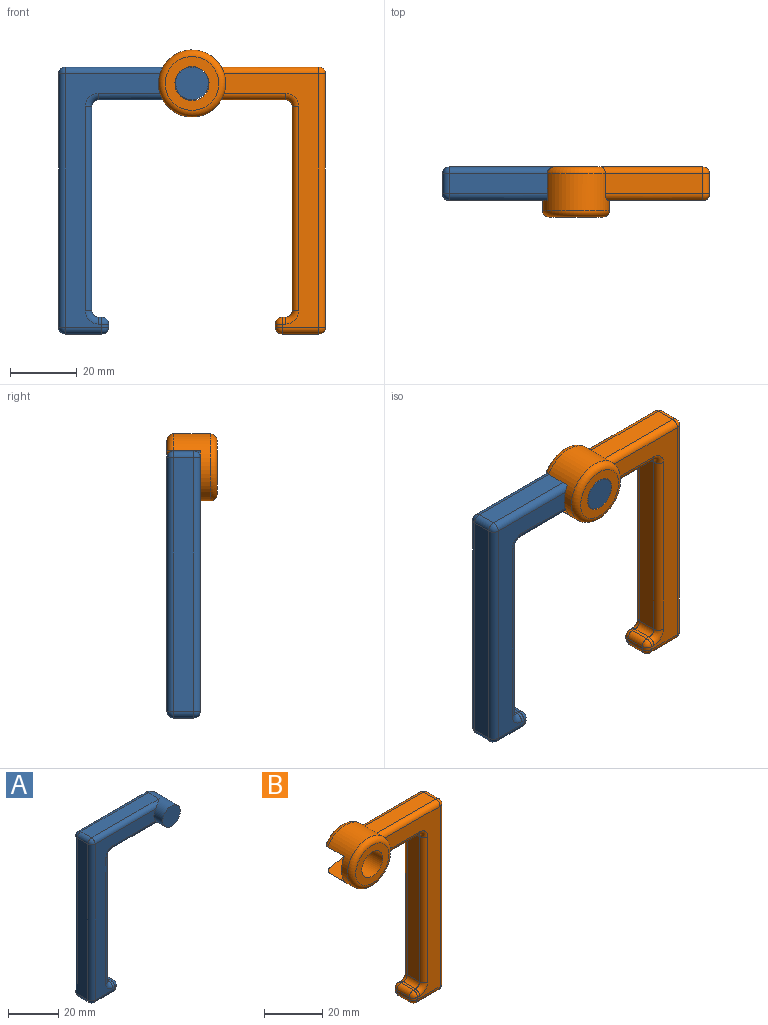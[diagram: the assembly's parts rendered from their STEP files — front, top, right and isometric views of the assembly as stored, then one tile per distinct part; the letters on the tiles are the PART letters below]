
ASSEMBLY  parts=2 mates=1
PART A: 44 faces, bbox 45.3x15x80.4 mm
  f0: cylinder r=2mm len=6mm, axis (0,1,0), area 18.8mm2, adj f1,f11,f16,f21
  f1: plane 28x6mm, normal (0,0,-1), area 168mm2, adj f0,f2,f15,f25
  f2: cylinder r=4.9mm len=13mm, axis (0,1,0), area 284.1mm2, adj f1,f3,f12,f14,f15,f17,f29
  f3: plane 38x6mm, normal (0,0,1), area 228mm2, adj f2,f4,f17,f34
  f4: cylinder r=2mm len=6mm, axis (0,1,0), area 18.8mm2, adj f3,f5,f19,f37
  f5: plane 76x6mm, normal (-1,0,0), area 456mm2, adj f4,f6,f22,f40
  f6: cylinder r=2mm len=6mm, axis (0,1,0), area 18.8mm2, adj f5,f7,f26,f42
  f7: plane 11x6mm, normal (0,0,-1), area 66mm2, adj f6,f30,f38,f43
  f8: plane 6x1mm, normal (1,0,0), area 6mm2, adj f31,f32,f38,f39
  f9: plane 6x1mm, normal (0,0,1), area 6mm2, adj f10,f23,f32,f33
  f10: cylinder r=2mm len=6mm, axis (0,1,0), area 18.8mm2, adj f9,f11,f20,f28
  f11: plane 61.2x6mm, normal (1,0,0), area 367.2mm2, adj f0,f10,f18,f24
  f12: plane 76x34.05mm, normal (0,-1,0), area 626.8mm2, adj f2,f15,f16,f17,f18,f20,f22,f23
  f13: plane 76x40.9mm, normal (0,1,0), area 666.7mm2, adj f21,f24,f25,f28,f29,f33,f34,f39
  f14: plane 9.8x9.8mm, normal (0,-1,0), area 75.4mm2, adj f2
  f15: cylinder r=2mm len=28mm, axis (-1,0,0), area 81mm2, adj f1,f2,f12,f16
  f16: torus R=4mm, axis (0,-1,0), area 13.5mm2, adj f0,f12,f15,f18
  f17: cylinder r=2mm len=38mm, axis (1,0,0), area 112.5mm2, adj f2,f3,f12,f19
  f18: cylinder r=2mm len=61.2mm, axis (0,0,-1), area 192.3mm2, adj f11,f12,f16,f20
  f19: sphere r=2mm, area 6.3mm2, adj f4,f17,f22
  f20: torus R=4mm, axis (0,-1,0), area 13.5mm2, adj f10,f12,f18,f23
  f21: torus R=4mm, axis (0,-1,0), area 13.5mm2, adj f0,f13,f24,f25
  f22: cylinder r=2mm len=76mm, axis (0,0,1), area 238.8mm2, adj f5,f12,f19,f26
  f23: cylinder r=2mm len=2mm, axis (1,0,0), area 3.1mm2, adj f9,f12,f20,f27
  f24: cylinder r=2mm len=61.2mm, axis (0,0,1), area 192.3mm2, adj f11,f13,f21,f28
  f25: cylinder r=2mm len=28mm, axis (1,0,0), area 88mm2, adj f1,f13,f21,f29
  f26: sphere r=2mm, area 6.3mm2, adj f6,f22,f30
  f27: sphere r=2mm, area 6.3mm2, adj f23,f31,f32
  f28: torus R=4mm, axis (0,-1,0), area 13.5mm2, adj f10,f13,f24,f33
  f29: torus R=2.9mm, axis (0,-1,0), area 41.2mm2, adj f2,f13,f25,f34
  f30: cylinder r=2mm len=11mm, axis (-1,0,0), area 34.6mm2, adj f7,f12,f26,f35
  f31: cylinder r=2mm len=2mm, axis (0,0,-1), area 3.1mm2, adj f8,f12,f27,f35
  f32: cylinder r=2mm len=6mm, axis (0,1,0), area 18.8mm2, adj f8,f9,f27,f36
  f33: cylinder r=2mm len=2mm, axis (-1,0,0), area 3.1mm2, adj f9,f13,f28,f36
  f34: cylinder r=2mm len=38mm, axis (-1,0,0), area 119.4mm2, adj f3,f13,f29,f37
  f35: sphere r=2mm, area 6.3mm2, adj f30,f31,f38
  f36: sphere r=2mm, area 6.3mm2, adj f32,f33,f39
  f37: sphere r=2mm, area 6.3mm2, adj f4,f34,f40
  f38: cylinder r=2mm len=6mm, axis (0,1,0), area 18.8mm2, adj f7,f8,f35,f41
  f39: cylinder r=2mm len=2mm, axis (0,0,1), area 3.1mm2, adj f8,f13,f36,f41
  f40: cylinder r=2mm len=76mm, axis (0,0,-1), area 238.8mm2, adj f5,f13,f37,f42
  f41: sphere r=2mm, area 6.3mm2, adj f38,f39,f43
  f42: sphere r=2mm, area 6.3mm2, adj f6,f40,f43
  f43: cylinder r=2mm len=11mm, axis (1,0,0), area 34.6mm2, adj f7,f13,f41,f42
PART B: 50 faces, bbox 50.9x15x86 mm
  f0: cylinder r=5.1mm len=15mm, axis (0,1,0), area 320.4mm2, adj f2,f3,f4,f5,f6
  f1: cylinder r=10.05mm len=20.1mm, axis (0,1,0), area 515.7mm2, adj f3,f5,f6,f7,f15,f17,f19,f21
  f2: plane 16.1x16.1mm, normal (0,-1,0), area 121.9mm2, adj f0,f49
  f3: plane 11.56x10.05mm, normal (0,1,0), area 63mm2, adj f0,f1,f5,f6
  f4: plane 81.15x44.23mm, normal (0,1,0), area 691.4mm2, adj f0,f5,f6,f19,f20,f21,f22,f23
  f5: plane 10x7.7mm, normal (-0.17,0,0.98), area 77.2mm2, adj f0,f1,f3,f4,f19
  f6: plane 10x8.66mm, normal (0,0,-1), area 85.6mm2, adj f0,f1,f3,f4,f21
  f7: plane 76x28.38mm, normal (0,-1,0), area 596mm2, adj f1,f25,f28,f31,f34,f38,f39,f44
  f8: cylinder r=2mm len=6mm, axis (0,1,0), area 18.8mm2, adj f9,f16,f32,f47
  f9: plane 11x6mm, normal (0,0,-1), area 66mm2, adj f8,f35,f43,f48
  f10: plane 6x1mm, normal (-1,0,0), area 6mm2, adj f36,f37,f43,f44
  f11: plane 6x1mm, normal (0,0,1), area 6mm2, adj f12,f30,f37,f38
  f12: cylinder r=2mm len=6mm, axis (0,1,0), area 18.8mm2, adj f11,f13,f27,f34
  f13: plane 61.2x6mm, normal (-1,0,0), area 367.2mm2, adj f12,f14,f24,f31
  f14: cylinder r=2mm len=6mm, axis (0,1,0), area 18.8mm2, adj f13,f15,f22,f28
  f15: plane 19.23x6mm, normal (0,0,-1), area 115.4mm2, adj f1,f14,f20,f25
  f16: plane 76x6mm, normal (1,0,0), area 456mm2, adj f8,f18,f29,f45
  f17: plane 29.23x6mm, normal (0,0,1), area 175.4mm2, adj f1,f18,f23,f39
  f18: cylinder r=2mm len=6mm, axis (0,1,0), area 18.8mm2, adj f16,f17,f26,f42
  f19: torus R=8.05mm, axis (0,-1,0), area 56.6mm2, adj f1,f4,f5,f20
  f20: cylinder r=2mm len=20.49mm, axis (1,0,0), area 61.8mm2, adj f4,f15,f19,f22
  f21: torus R=8.05mm, axis (0,-1,0), area 61.4mm2, adj f1,f4,f6,f23
  f22: torus R=4mm, axis (0,-1,0), area 13.5mm2, adj f4,f14,f20,f24
  f23: cylinder r=2mm len=30.49mm, axis (-1,0,0), area 93.2mm2, adj f4,f17,f21,f26
  f24: cylinder r=2mm len=61.2mm, axis (0,0,-1), area 192.3mm2, adj f4,f13,f22,f27
  f25: cylinder r=2mm len=19.23mm, axis (-1,0,0), area 59.3mm2, adj f1,f7,f15,f28
  f26: sphere r=2mm, area 6.3mm2, adj f18,f23,f29
  f27: torus R=4mm, axis (0,-1,0), area 13.5mm2, adj f4,f12,f24,f30
  f28: torus R=4mm, axis (0,-1,0), area 13.5mm2, adj f7,f14,f25,f31
  f29: cylinder r=2mm len=76mm, axis (0,0,1), area 238.8mm2, adj f4,f16,f26,f32
  f30: cylinder r=2mm len=2mm, axis (-1,0,0), area 3.1mm2, adj f4,f11,f27,f33
  f31: cylinder r=2mm len=61.2mm, axis (0,0,1), area 192.3mm2, adj f7,f13,f28,f34
  f32: sphere r=2mm, area 6.3mm2, adj f8,f29,f35
  f33: sphere r=2mm, area 6.3mm2, adj f30,f36,f37
  f34: torus R=4mm, axis (0,-1,0), area 13.5mm2, adj f7,f12,f31,f38
  f35: cylinder r=2mm len=11mm, axis (1,0,0), area 34.6mm2, adj f4,f9,f32,f40
  f36: cylinder r=2mm len=2mm, axis (0,0,-1), area 3.1mm2, adj f4,f10,f33,f40
  f37: cylinder r=2mm len=6mm, axis (0,1,0), area 18.8mm2, adj f10,f11,f33,f41
  f38: cylinder r=2mm len=2mm, axis (1,0,0), area 3.1mm2, adj f7,f11,f34,f41
  f39: cylinder r=2mm len=29.23mm, axis (1,0,0), area 90.7mm2, adj f1,f7,f17,f42
  f40: sphere r=2mm, area 6.3mm2, adj f35,f36,f43
  f41: sphere r=2mm, area 6.3mm2, adj f37,f38,f44
  f42: sphere r=2mm, area 6.3mm2, adj f18,f39,f45
  f43: cylinder r=2mm len=6mm, axis (0,1,0), area 18.8mm2, adj f9,f10,f40,f46
  f44: cylinder r=2mm len=2mm, axis (0,0,1), area 3.1mm2, adj f7,f10,f41,f46
  f45: cylinder r=2mm len=76mm, axis (0,0,-1), area 238.8mm2, adj f7,f16,f42,f47
  f46: sphere r=2mm, area 6.3mm2, adj f43,f44,f48
  f47: sphere r=2mm, area 6.3mm2, adj f8,f45,f48
  f48: cylinder r=2mm len=11mm, axis (-1,0,0), area 34.6mm2, adj f7,f9,f46,f47
  f49: torus R=8.05mm, axis (0,-1,0), area 184mm2, adj f1,f2
PLACE A rot(axis=(1,0,0),0deg) t=(10.91,15.8,-15.57)mm
PLACE B t=(10.91,15.8,-15.57)mm fixed
MATE revolute A.f2 <-> B.f0  axis (0,-1,0) through (20.91,0.8,9.33)mm
